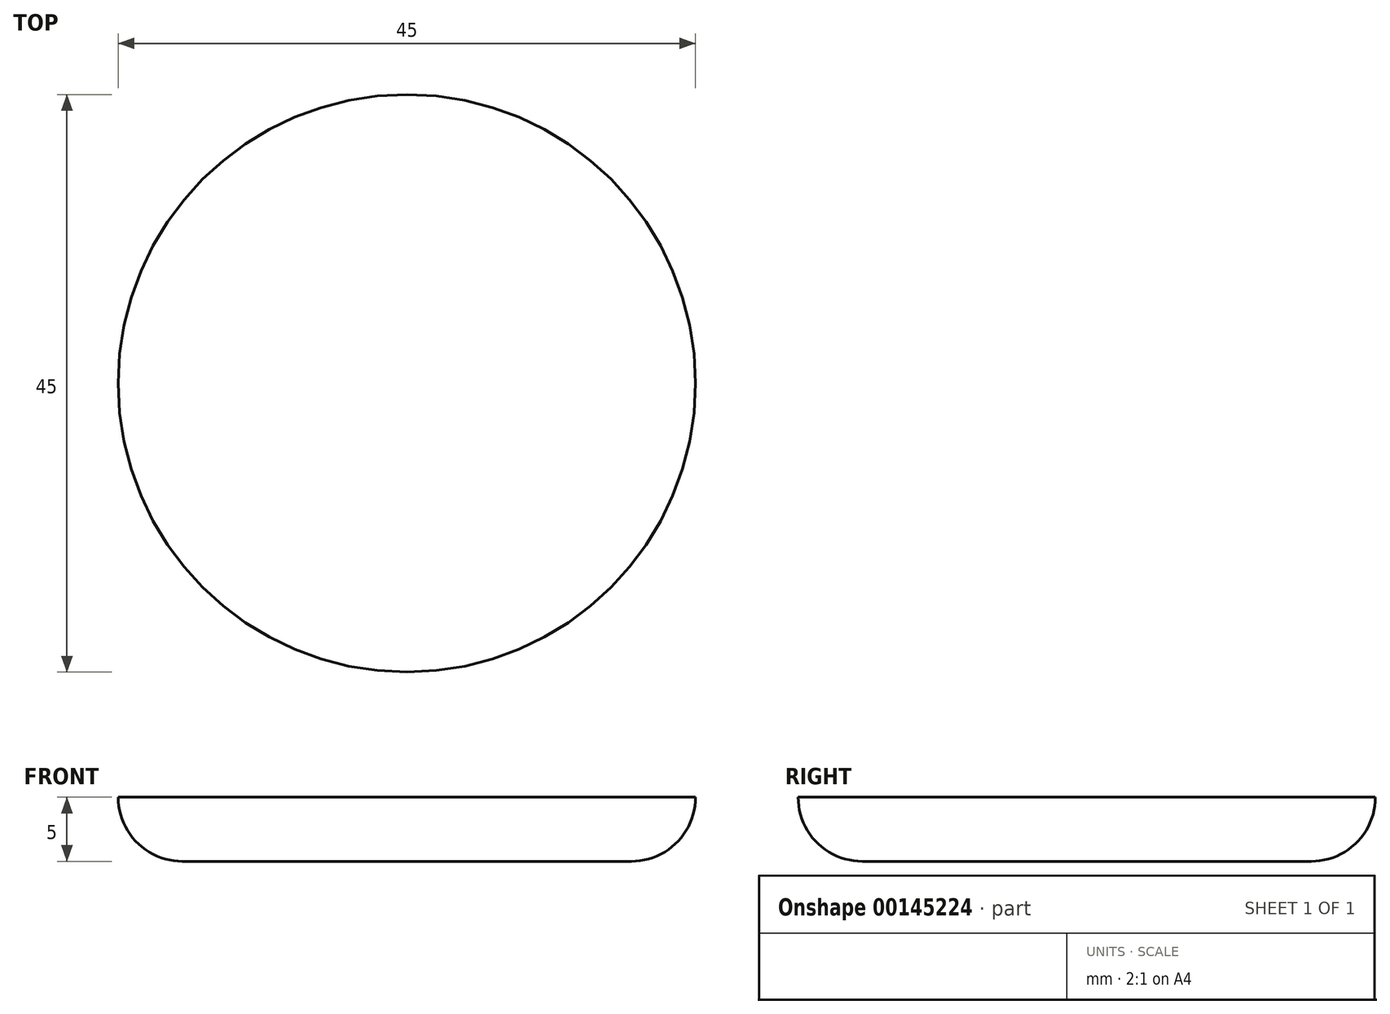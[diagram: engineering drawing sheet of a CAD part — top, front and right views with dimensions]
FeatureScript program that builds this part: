
annotation { "Feature Type Name" : "Feature", "Feature Type Description" : "" }
export const myFeature = defineFeature(function(context is Context, id is Id, definition is map)
    precondition{}
    {
        {
            var Q0;
            Q0=qCreatedBy(makeId("Top.planeOp"),FACE);
            var sketch = newSketch(context, id + "F0", { "sketchPlane" : qUnion([Q0])});
            skCircle(sketch, "E0", {"center": v(0, 0) * mm, "radius": 22.5 * mm});
            skSolve(sketch);
        }
        {
            var Q0;
            Q0 = qSketchRegion(id + "F0", true);
            extrude(context, id + "F1", {"entities" : qUnion([Q0]), "depth" : 5 * mm});
        }
        {
            var Q0;
            Q0=makeQuery(id+"F1.opExtrude","CAP_EDGE",EDGE,{"disambiguationData":[OSD([sQuery(id+"F0.wireOp",EDGE,"E0")])],"isStart":true});
            fillet(context, id + "F2", {"entities" : qUnion([Q0]), "radius" : 5 * mm, "tangentPropagation" : true, "allowEdgeOverflow" : false});
        }
    });
